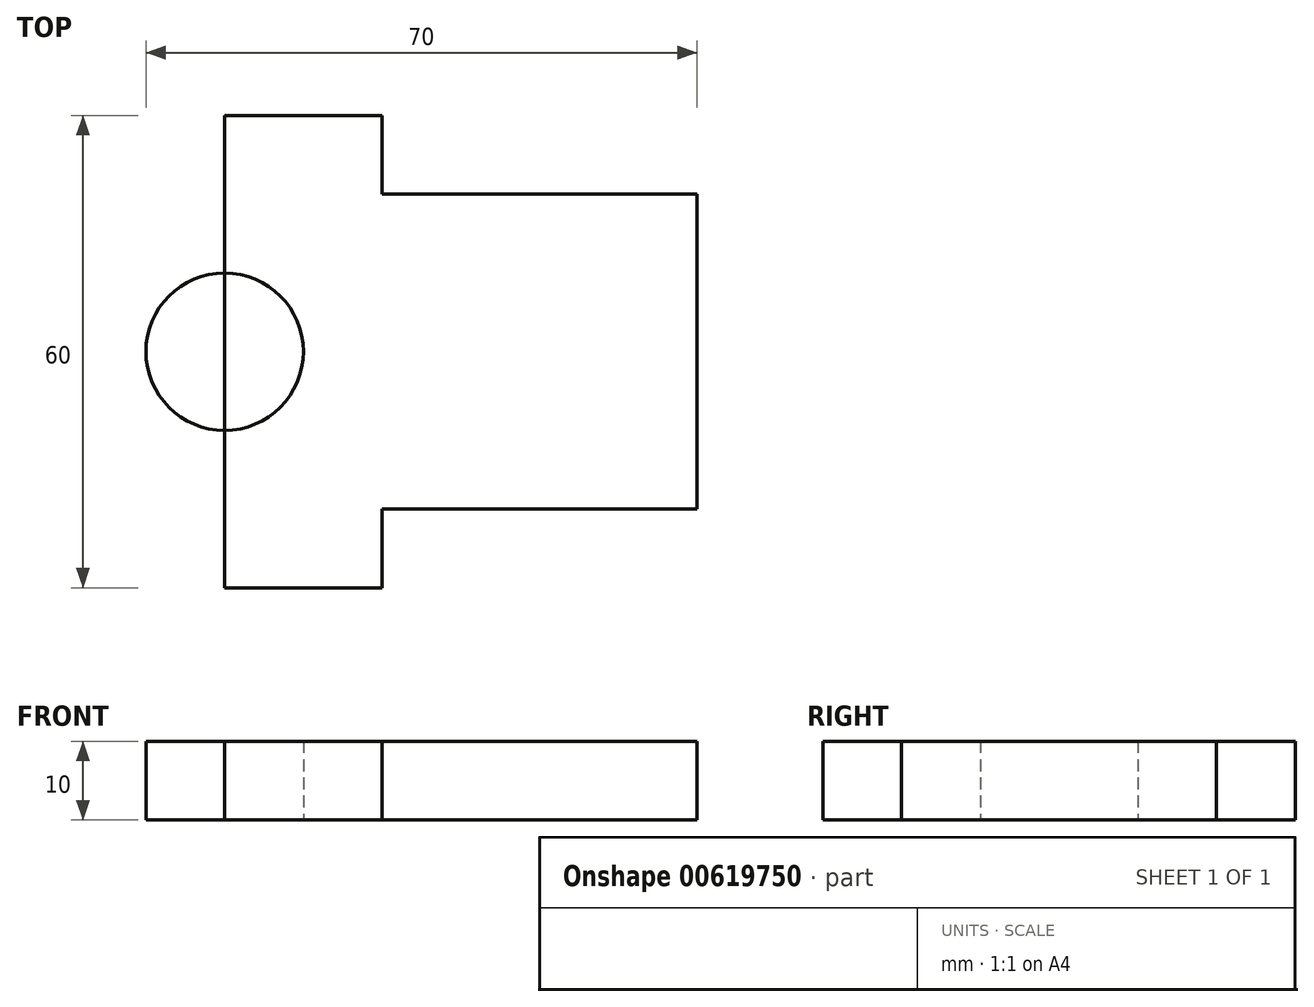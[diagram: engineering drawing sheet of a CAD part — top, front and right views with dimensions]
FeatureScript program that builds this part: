
annotation { "Feature Type Name" : "Feature", "Feature Type Description" : "" }
export const myFeature = defineFeature(function(context is Context, id is Id, definition is map)
    precondition{}
    {
        {
            var Q0;
            Q0=qCreatedBy(makeId("Top.planeOp"),FACE);
            var sketch = newSketch(context, id + "F0", { "sketchPlane" : qUnion([Q0])});
            skLineSegment(sketch, "E0", {"start": v(0, 0) * mm, "end": v(0, 45.66) * mm, "construction": true});
            skLineSegment(sketch, "E1", {"start": v(0, 0) * mm, "end": v(0, -30) * mm, "construction": true});
            skArc(sketch, "E2", {"start": v(0, -10) * mm, "mid": v(10, 0) * mm, "end": v(0, 10) * mm});
            skArc(sketch, "E3.MirrorCS", {"start": v(0, -10) * mm, "mid": v(-10, 0) * mm, "end": v(0, 10) * mm});
            skArc(sketch, "E4", {"start": v(0, 30) * mm, "mid": v(-30, 0) * mm, "end": v(0, -30) * mm});
            skLineSegment(sketch, "E5.bottom", {"start": v(0, 30) * mm, "end": v(20, 30) * mm});
            skLineSegment(sketch, "E5.left", {"start": v(0, 30) * mm, "end": v(0, -30) * mm});
            skLineSegment(sketch, "E5.right", {"start": v(60, 20) * mm, "end": v(60, -20) * mm});
            skLineSegment(sketch, "E6", {"start": v(0, 0) * mm, "end": v(66.71, 0) * mm});
            skPoint(sketch, "E6.endSnap0", {"position": v(-30, 0) * mm});
            skLineSegment(sketch, "E7.top", {"start": v(60, 20) * mm, "end": v(20, 20) * mm});
            skLineSegment(sketch, "E7.right", {"start": v(20, 30) * mm, "end": v(20, 20) * mm});
            skLineSegment(sketch, "E8.MirrorCS", {"start": v(60, -20) * mm, "end": v(20, -20) * mm});
            skLineSegment(sketch, "E9.MirrorCS", {"start": v(20, -30) * mm, "end": v(20, -20) * mm});
            skLineSegment(sketch, "E10.MirrorCS", {"start": v(0, -30) * mm, "end": v(20, -30) * mm});
            skPoint(sketch, "E11.MirrorCS.end.orphan", {"position": v(20, -30) * mm});
            skSolve(sketch);
        }
        {
            var Q0;
            {var subQ0=sQuery(id+"F0.wireOp",EDGE,"E3.MirrorCS");Q0=makeQuery(id+"F0.imprint","IMPRINT",FACE,{"disambiguationData":[TD([[makeQuery(id+"F0.imprint","IMPRINT",EDGE,{"derivedFrom":subQ0}),1.0]])]});}
            var Q1;
            {var subQ3=sQuery(id+"F0.wireOp",EDGE,"E5.bottom");Q1=makeQuery(id+"F0.imprint","IMPRINT",FACE,{"disambiguationData":[TD([[makeQuery(id+"F0.imprint","IMPRINT",EDGE,{"derivedFrom":subQ3}),-1.0]])]});}
            var Q2;
            {var subQ8=sQuery(id+"F0.wireOp",EDGE,"E8.MirrorCS");Q2=makeQuery(id+"F0.imprint","IMPRINT",FACE,{"disambiguationData":[TD([[makeQuery(id+"F0.imprint","IMPRINT",EDGE,{"derivedFrom":subQ8}),-1.0]])]});}
            extrude(context, id + "F1", {"entities" : qUnion([Q0, Q1, Q2]), "depth" : 10 * mm, "offsetDistance" : 25 * mm});
        }
    });
